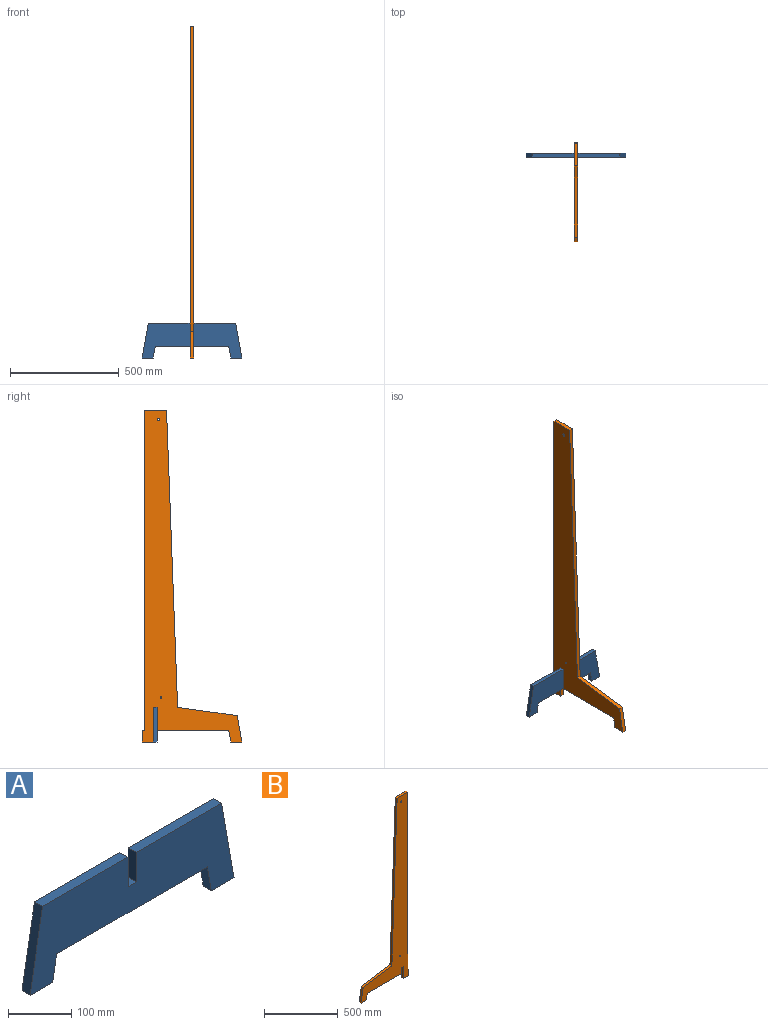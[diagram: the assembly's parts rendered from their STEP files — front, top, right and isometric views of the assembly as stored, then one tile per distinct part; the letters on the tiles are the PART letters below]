
ASSEMBLY  parts=2 mates=1
PART A: 14 faces, bbox 457.2x18x158.8 mm
  f0: plane 191.59x18.03mm, normal (0,0,1), area 3455.2mm2, adj f1,f11,f12,f13
  f1: plane 57.15x18.03mm, normal (-1,0,0), area 1030.6mm2, adj f0,f2,f12,f13
  f2: plane 18.03x18.03mm, normal (0,0,1), area 325.2mm2, adj f1,f3,f12,f13
  f3: plane 57.15x18.03mm, normal (1,0,0), area 1030.6mm2, adj f2,f4,f12,f13
  f4: plane 191.59x18.03mm, normal (0,0,1), area 3455.2mm2, adj f3,f5,f12,f13
  f5: plane 158.75x27.99mm, normal (-0.98,0,0.17), area 2907.1mm2, adj f4,f6,f12,f13
  f6: plane 50.8x18.03mm, normal (0,0,-1), area 916.1mm2, adj f5,f7,f12,f13
  f7: plane 50.8x18.03mm, normal (0.98,0,-0.17), area 930.3mm2, adj f6,f8,f12,f13
  f8: plane 337.69x18.03mm, normal (0,0,-1), area 6089.8mm2, adj f7,f9,f12,f13
  f9: plane 50.8x18.03mm, normal (-0.98,0,-0.17), area 930.3mm2, adj f8,f10,f12,f13
  f10: plane 50.8x18.03mm, normal (0,0,-1), area 916.1mm2, adj f9,f11,f12,f13
  f11: plane 158.75x27.99mm, normal (0.98,0,0.17), area 2907.1mm2, adj f0,f10,f12,f13
  f12: plane 457.2x158.75mm, normal (0,-1,0), area 49496.7mm2, adj f0,f1,f2,f3,f4,f5,f6,f7
  f13: plane 457.2x158.75mm, normal (0,1,0), area 49496.7mm2, adj f0,f1,f2,f3,f4,f5,f6,f7
PART B: 18 faces, bbox 457.2x18x1524 mm
  f0: plane 273.31x37.77mm, normal (-0.14,0,0.99), area 4975.7mm2, adj f1,f15,f16,f17
  f1: plane 120.98x21.33mm, normal (-0.98,0,0.17), area 2215.3mm2, adj f0,f2,f16,f17
  f2: plane 50.8x18.03mm, normal (0,0,-1), area 916.1mm2, adj f1,f3,f16,f17
  f3: plane 50.8x18.03mm, normal (0.98,0,-0.17), area 930.3mm2, adj f2,f4,f16,f17
  f4: plane 328.61x18.03mm, normal (0,0,-1), area 5926.1mm2, adj f3,f5,f16,f17
  f5: plane 50.8x18.03mm, normal (1,0,0), area 916.1mm2, adj f4,f6,f16,f17
  f6: plane 18.03x18.03mm, normal (0,0,-1), area 325.2mm2, adj f5,f7,f16,f17
  f7: plane 101.6x18.03mm, normal (-1,0,0), area 1832.3mm2, adj f6,f8,f16,f17
  f8: plane 50.8x18.03mm, normal (0,0,-1), area 916.1mm2, adj f7,f9,f16,f17
  f9: plane 50.8x18.03mm, normal (1,0,0), area 916.1mm2, adj f8,f10,f16,f17
  f10: plane 18.03x10.16mm, normal (0,0,1), area 183.2mm2, adj f9,f11,f16,f17
  f11: plane 1473.2x18.03mm, normal (1,0,0), area 26567.7mm2, adj f10,f12,f16,f17
  f12: plane 101.6x18.03mm, normal (0,0,1), area 1832.3mm2, adj f11,f15,f16,f17
  f13: cylinder r=3.81mm len=18.03mm, axis (0,1,0), area 431.7mm2, adj f16,f17
  f14: cylinder r=5.59mm len=18.03mm, axis (0,1,0), area 633.2mm2, adj f16,f17
  f15: plane 1365.25x50.8mm, normal (-1,0,0.04), area 24638mm2, adj f0,f12,f16,f17
  f16: plane 1524x457.2mm, normal (0,-1,0), area 218715.6mm2, adj f0,f1,f2,f3,f4,f5,f6,f7
  f17: plane 1524x457.2mm, normal (0,1,0), area 218715.6mm2, adj f0,f1,f2,f3,f4,f5,f6,f7
PLACE A t=(-756.89,45.88,-64.21)mm
PLACE B rot(axis=(0,0,1),90deg) t=(-400.15,86.52,-64.21)mm
MATE fastened B.f6 <-> A.f2  axis (0,0,-1) through (-391.13,36.86,-13.41)mm
